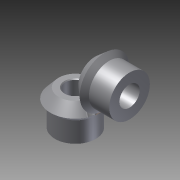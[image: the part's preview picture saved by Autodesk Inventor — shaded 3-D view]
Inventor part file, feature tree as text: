
AUTODESK INVENTOR PART (.ipt)
format: ipt  version: 2012 (Build 160160000, 160)  size: 465,920 bytes
history: native  units: in
note: dims shown in document units (in); Inventor stores cm internally (conversion verified against a paired STEP export)
features: extrude x2, imported_body x2, sketch x2, other x2
ambient origin geometry x8: Origin, YZ Plane, XZ Plane, XY Plane, X Axis, Y Axis, Z Axis, Center Point
feature tree (8):
  extrude  "Extrusion1"  Depth=0.125in TaperAngle=0.0deg
  extrude  "Extrusion2"  [1 undecoded]
  imported_body  "Base1"
  imported_body  "Base2"
  sketch  "Sketch2"  dims[d0=0.125in d1=0.0in d2=0.125in d3=0.0in]
  sketch  "Sketch3"
  other  "Composite1"
  other  "Srf1"
note: 1 required parameter value undecoded (feature->parameter linkage not recoverable at this tier; creation-order binding heuristic only, values carry confidence <= 0.55)
